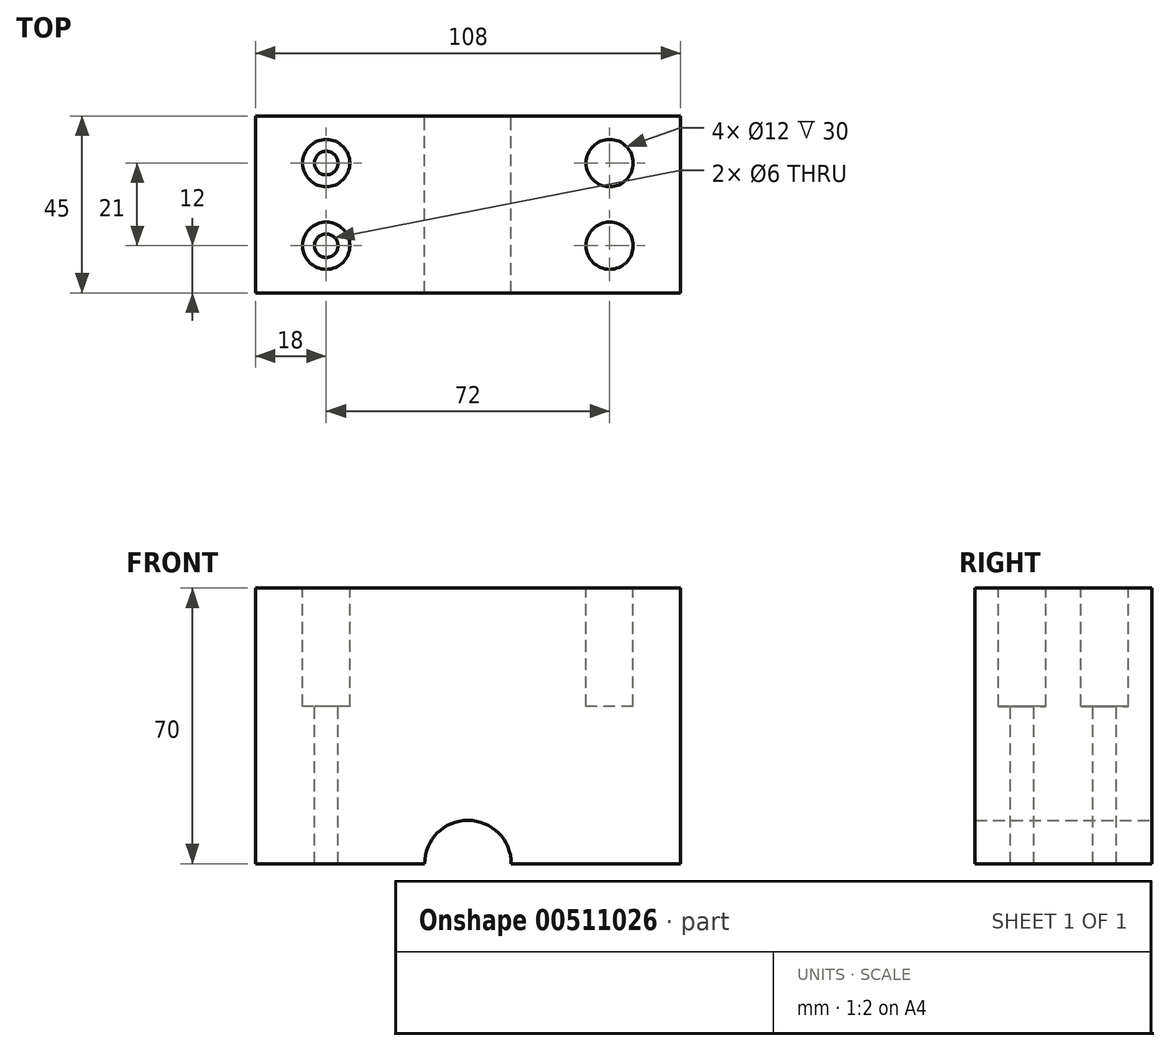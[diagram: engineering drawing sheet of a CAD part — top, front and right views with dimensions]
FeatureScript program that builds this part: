
annotation { "Feature Type Name" : "Feature", "Feature Type Description" : "" }
export const myFeature = defineFeature(function(context is Context, id is Id, definition is map)
    precondition{}
    {
        {
            var Q0;
            Q0=qCreatedBy(makeId("Front.planeOp"),FACE);
            var sketch = newSketch(context, id + "F0", { "sketchPlane" : qUnion([Q0])});
            skLineSegment(sketch, "E0.bottom", {"start": v(0, 0) * mm, "end": v(-43, 0) * mm});
            skLineSegment(sketch, "E0.top", {"start": v(0, 70) * mm, "end": v(-108, 70) * mm});
            skLineSegment(sketch, "E0.left", {"start": v(0, 0) * mm, "end": v(0, 70) * mm});
            skLineSegment(sketch, "E0.right", {"start": v(-108, 0) * mm, "end": v(-108, 70) * mm});
            skArc(sketch, "E1", {"start": v(-43, 0) * mm, "mid": v(-54, 11) * mm, "end": v(-65, 0) * mm});
            skLineSegment(sketch, "E2.trimOffspring", {"start": v(-65, 0) * mm, "end": v(-108, 0) * mm});
            skSolve(sketch);
        }
        {
            var Q0;
            Q0=qSketchRegion(id+"F0",true);
            extrude(context, id + "F1", {"entities" : qUnion([Q0]), "depth" : 45 * mm});
        }
        {
            var Q0;
            Q0=makeQuery(id+"F1.opExtrude","SWEPT_FACE",FACE,{"disambiguationData":[OSD([sQuery(id+"F0.wireOp",EDGE,"E0.top")])]});
            var sketch = newSketch(context, id + "F2", { "sketchPlane" : qUnion([Q0])});
            skCircle(sketch, "E3", {"center": v(-90, -12) * mm, "radius": 6 * mm});
            skCircle(sketch, "E4", {"center": v(-90, -33) * mm, "radius": 6 * mm});
            skLineSegment(sketch, "E5", {"start": v(-90, -45) * mm, "end": v(-90, 0) * mm, "construction": true});
            skLineSegment(sketch, "E6", {"start": v(-54, 0) * mm, "end": v(-54, -45) * mm, "construction": true});
            skLineSegment(sketch, "E7.MirrorCS", {"start": v(-18, -45) * mm, "end": v(-18, 0) * mm, "construction": true});
            skCircle(sketch, "E8.MirrorC", {"center": v(-18, -12) * mm, "radius": 6 * mm});
            skCircle(sketch, "E9.MirrorC", {"center": v(-18, -33) * mm, "radius": 6 * mm});
            skSolve(sketch);
        }
        {
            var Q0;
            Q0=qSketchRegion(id+"F2",true);
            extrude(context, id + "F3", {"entities" : qUnion([Q0]), "operationType" : NewBodyOperationType.REMOVE, "oppositeDirection" : true, "depth" : 30 * mm});
        }
        {
            var Q0;
            Q0=makeQuery(id+"F3.boolean.opBoolean","COPY",FACE,{"derivedFrom":makeQuery(id+"F3.opExtrude","CAP_FACE",FACE,{"disambiguationData":[OSD([sQuery(id+"F2.wireOp",EDGE,"E4")])],"isStart":false})});
            var sketch = newSketch(context, id + "F4", { "sketchPlane" : qUnion([Q0])});
            skCircle(sketch, "E10", {"center": v(-90, -33) * mm, "radius": 3 * mm});
            skCircle(sketch, "E11", {"center": v(-90, -12) * mm, "radius": 3 * mm});
            skLineSegment(sketch, "E12.0", {"start": v(0, 0) * mm, "end": v(-108, 0) * mm, "construction": true});
            skLineSegment(sketch, "E13", {"start": v(-54, 0) * mm, "end": v(-54, -41.58) * mm, "construction": true});
            skCircle(sketch, "E14.MirrorC", {"center": v(-18, -12) * mm, "radius": 3 * mm});
            skCircle(sketch, "E15.MirrorC", {"center": v(-18, -33) * mm, "radius": 3 * mm});
            skSolve(sketch);
        }
        {
            var Q0;
            Q0=makeQuery(id+"F4.imprint","IMPRINT",FACE,{"disambiguationData":[TD([[makeQuery(id+"F4.imprint","IMPRINT",EDGE,{"derivedFrom":sQuery(id+"F4.wireOp",EDGE,"E11")}),1.0]])]});
            var Q1;
            Q1=makeQuery(id+"F4.imprint","IMPRINT",FACE,{"disambiguationData":[TD([[makeQuery(id+"F4.imprint","IMPRINT",EDGE,{"derivedFrom":sQuery(id+"F4.wireOp",EDGE,"E14.MirrorC")}),-1.0]])]});
            var Q2;
            Q2=makeQuery(id+"F4.imprint","IMPRINT",FACE,{"disambiguationData":[TD([[makeQuery(id+"F4.imprint","IMPRINT",EDGE,{"derivedFrom":sQuery(id+"F4.wireOp",EDGE,"E15.MirrorC")}),-1.0]])]});
            var Q3;
            Q3=makeQuery(id+"F4.imprint","IMPRINT",FACE,{"disambiguationData":[TD([[makeQuery(id+"F4.imprint","IMPRINT",EDGE,{"derivedFrom":sQuery(id+"F4.wireOp",EDGE,"E10")}),1.0]])]});
            extrude(context, id + "F5", {"entities" : qUnion([Q0, Q1, Q2, Q3]), "operationType" : NewBodyOperationType.REMOVE, "endBound" : BoundingType.THROUGH_ALL, "oppositeDirection" : true, "depth" : 25 * mm});
        }
    });
